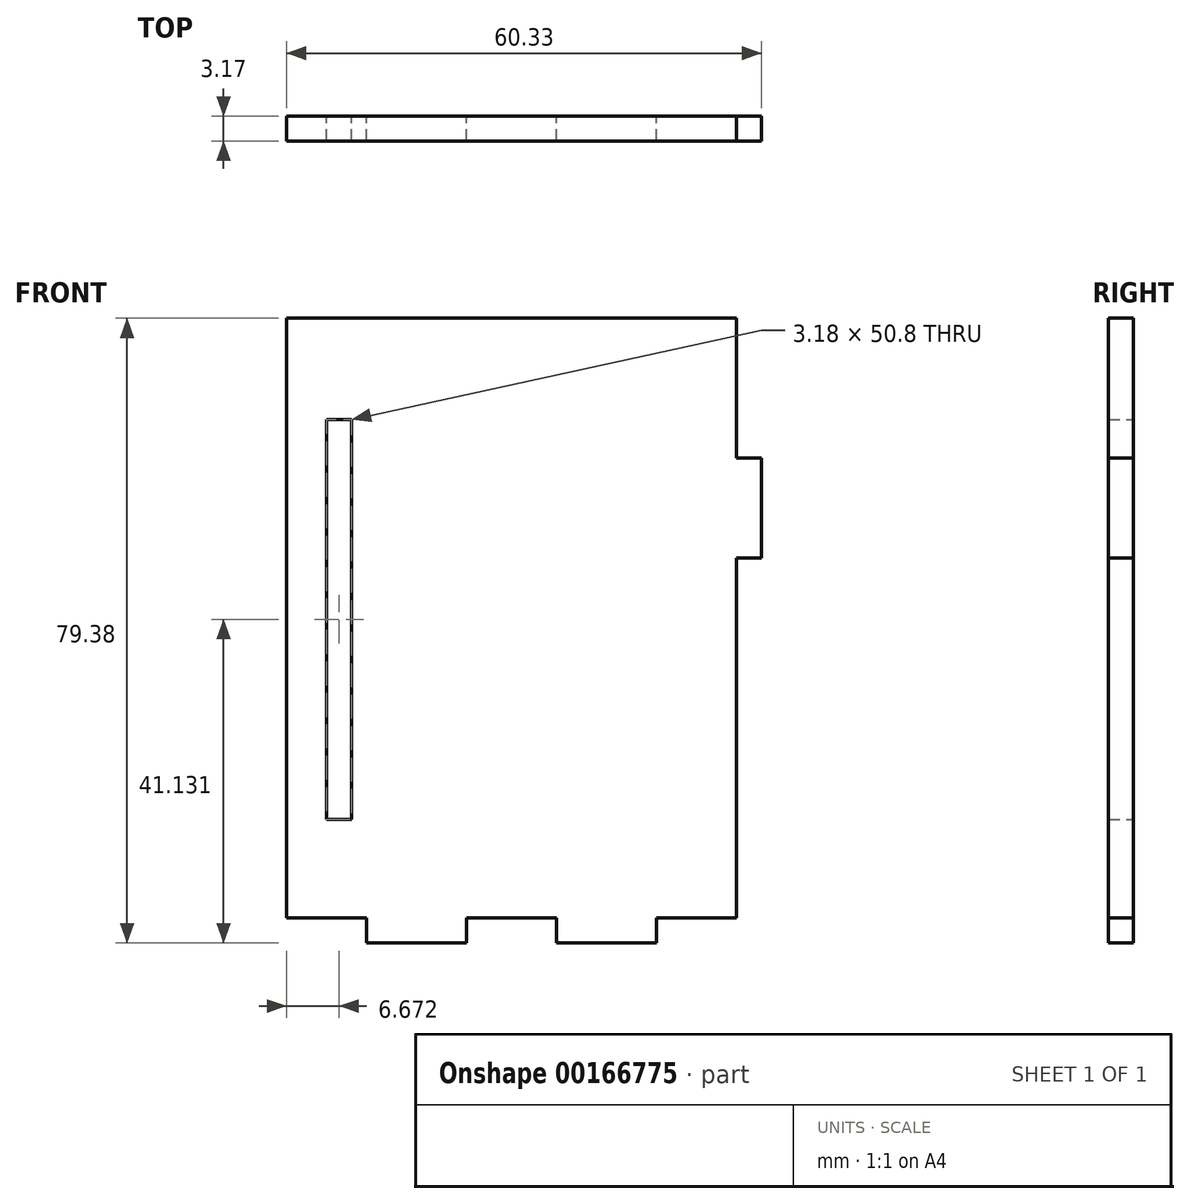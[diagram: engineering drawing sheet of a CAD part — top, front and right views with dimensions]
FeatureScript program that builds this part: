
annotation { "Feature Type Name" : "Feature", "Feature Type Description" : "" }
export const myFeature = defineFeature(function(context is Context, id is Id, definition is map)
    precondition{}
    {
        {
            var Q0;
            Q0=qCreatedBy(makeId("Front.planeOp"),FACE);
            var sketch = newSketch(context, id + "F0", { "sketchPlane" : qUnion([Q0])});
            skLineSegment(sketch, "E0.bottom", {"start": v(-29.7, 30.48) * mm, "end": v(27.45, 30.48) * mm});
            skLineSegment(sketch, "E0.top", {"start": v(-29.7, -45.72) * mm, "end": v(27.45, -45.72) * mm});
            skLineSegment(sketch, "E0.left", {"start": v(-29.7, 30.48) * mm, "end": v(-29.7, -45.72) * mm});
            skLineSegment(sketch, "E0.right", {"start": v(27.45, 30.48) * mm, "end": v(27.45, 12.7) * mm});
            skLineSegment(sketch, "E1", {"start": v(-19.54, -45.72) * mm, "end": v(-19.54, -48.9) * mm});
            skLineSegment(sketch, "E2", {"start": v(-19.54, -48.9) * mm, "end": v(-6.84, -48.9) * mm});
            skLineSegment(sketch, "E3", {"start": v(-6.84, -48.9) * mm, "end": v(-6.84, -45.72) * mm});
            skLineSegment(sketch, "E4", {"start": v(-6.84, -45.72) * mm, "end": v(4.6, -45.72) * mm});
            skLineSegment(sketch, "E5", {"start": v(4.6, -45.72) * mm, "end": v(4.6, -48.9) * mm});
            skLineSegment(sketch, "E6", {"start": v(4.6, -48.9) * mm, "end": v(17.3, -48.9) * mm});
            skLineSegment(sketch, "E7", {"start": v(17.3, -48.9) * mm, "end": v(17.3, -45.72) * mm});
            skLineSegment(sketch, "E8.bottom", {"start": v(-24.62, 17.63) * mm, "end": v(-21.44, 17.63) * mm});
            skLineSegment(sketch, "E8.top", {"start": v(-24.62, -33.17) * mm, "end": v(-21.44, -33.17) * mm});
            skLineSegment(sketch, "E8.left", {"start": v(-24.62, 17.63) * mm, "end": v(-24.62, -33.17) * mm});
            skLineSegment(sketch, "E8.right", {"start": v(-21.44, 17.63) * mm, "end": v(-21.44, -33.17) * mm});
            skLineSegment(sketch, "E9.trimOffspring", {"start": v(27.45, 0) * mm, "end": v(27.45, -45.72) * mm});
            skLineSegment(sketch, "E10", {"start": v(27.45, 12.7) * mm, "end": v(27.45, 0) * mm});
            skLineSegment(sketch, "E11", {"start": v(27.45, 12.7) * mm, "end": v(30.63, 12.7) * mm});
            skLineSegment(sketch, "E12", {"start": v(30.63, 12.7) * mm, "end": v(30.63, 0) * mm});
            skLineSegment(sketch, "E13", {"start": v(30.63, 0) * mm, "end": v(27.45, 0) * mm});
            skSolve(sketch);
        }
        {
            var Q0;
            Q0=makeQuery(id+"F0.imprint","IMPRINT",FACE,{"disambiguationData":[TD([[makeQuery(id+"F0.imprint","IMPRINT",EDGE,{"derivedFrom":sQuery(id+"F0.wireOp",EDGE,"E0.bottom")}),-1.0]])]});
            var Q1;
            {var subQ0=sQuery(id+"F0.wireOp",EDGE,"E1");Q1=makeQuery(id+"F0.imprint","IMPRINT",FACE,{"disambiguationData":[TD([[makeQuery(id+"F0.imprint","IMPRINT",EDGE,{"derivedFrom":subQ0}),1.0]])]});}
            var Q2;
            {var subQ0=sQuery(id+"F0.wireOp",EDGE,"E5");Q2=makeQuery(id+"F0.imprint","IMPRINT",FACE,{"disambiguationData":[TD([[makeQuery(id+"F0.imprint","IMPRINT",EDGE,{"derivedFrom":subQ0}),1.0]])]});}
            var Q3;
            Q3=makeQuery(id+"F0.imprint","IMPRINT",FACE,{"disambiguationData":[TD([[makeQuery(id+"F0.imprint","IMPRINT",EDGE,{"derivedFrom":sQuery(id+"F0.wireOp",EDGE,"E10")}),1.0]])]});
            extrude(context, id + "F1", {"entities" : qUnion([Q0, Q1, Q2, Q3]), "depth" : 3.17 * mm});
        }
    });
